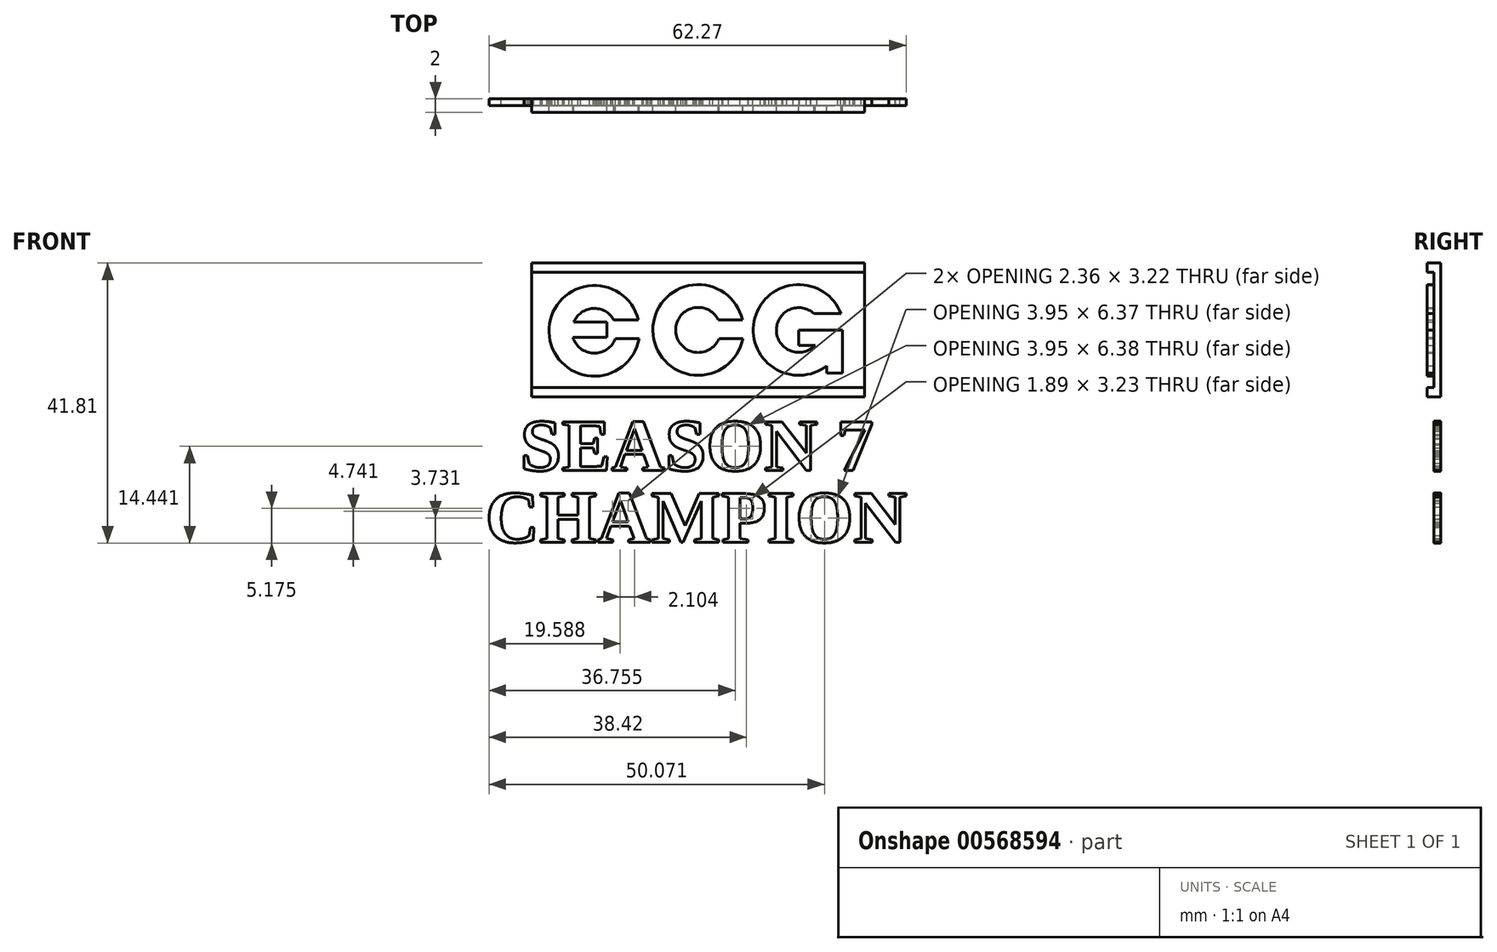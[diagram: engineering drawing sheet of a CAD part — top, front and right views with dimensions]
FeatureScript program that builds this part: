
annotation { "Feature Type Name" : "Feature", "Feature Type Description" : "" }
export const myFeature = defineFeature(function(context is Context, id is Id, definition is map)
    precondition{}
    {
        {
            var Q0;
            Q0=qCreatedBy(makeId("Front.planeOp"),FACE);
            var sketch = newSketch(context, id + "F0", { "sketchPlane" : qUnion([Q0])});
            skArc(sketch, "E0", {"start": v(-20.49, -35.74) * mm, "mid": v(-33.84, -37.62) * mm, "end": v(-20.4, -38.57) * mm});
            skArc(sketch, "E1", {"start": v(-4.95, -35.74) * mm, "mid": v(-18.33, -37.37) * mm, "end": v(-4.9, -38.57) * mm});
            skArc(sketch, "E2", {"start": v(9.79, -34.84) * mm, "mid": v(-3.08, -35.45) * mm, "end": v(7.63, -42.6) * mm});
            skArc(sketch, "E3", {"start": v(-30.27, -38.34) * mm, "mid": v(-27.19, -40.73) * mm, "end": v(-23.94, -38.57) * mm});
            skArc(sketch, "E4", {"start": v(-8.55, -35.74) * mm, "mid": v(-14.92, -37.38) * mm, "end": v(-8.45, -38.57) * mm});
            skLineSegment(sketch, "E5", {"start": v(-25.17, -36.06) * mm, "end": v(-25.17, -38.34) * mm});
            skLineSegment(sketch, "E6", {"start": v(3.45, -37.26) * mm, "end": v(3.45, -39.54) * mm});
            skLineSegment(sketch, "E7", {"start": v(7.63, -43.72) * mm, "end": v(9.99, -43.72) * mm});
            skLineSegment(sketch, "E8", {"start": v(-8.55, -35.74) * mm, "end": v(-4.95, -35.74) * mm});
            skLineSegment(sketch, "E9", {"start": v(-4.9, -38.57) * mm, "end": v(-8.45, -38.57) * mm});
            skLineSegment(sketch, "E10", {"start": v(-25.17, -36.06) * mm, "end": v(-30.13, -36.06) * mm});
            skLineSegment(sketch, "E11", {"start": v(-25.17, -38.34) * mm, "end": v(-30.27, -38.34) * mm});
            skLineSegment(sketch, "E12", {"start": v(-20.49, -35.74) * mm, "end": v(-24.16, -35.74) * mm});
            skLineSegment(sketch, "E13", {"start": v(-20.4, -38.57) * mm, "end": v(-23.94, -38.57) * mm});
            skArc(sketch, "E14.trimOffspring", {"start": v(-24.16, -35.74) * mm, "mid": v(-27.24, -34.05) * mm, "end": v(-30.13, -36.06) * mm});
            skArc(sketch, "E15", {"start": v(5.75, -34.84) * mm, "mid": v(0.12, -37.37) * mm, "end": v(5.9, -39.54) * mm});
            skLineSegment(sketch, "E16", {"start": v(6.8, -37.26) * mm, "end": v(3.45, -37.26) * mm});
            skLineSegment(sketch, "E17", {"start": v(3.45, -39.54) * mm, "end": v(5.9, -39.54) * mm});
            skLineSegment(sketch, "E18", {"start": v(5.75, -34.84) * mm, "end": v(9.79, -34.84) * mm});
            skLineSegment(sketch, "E19", {"start": v(6.8, -37.26) * mm, "end": v(9.99, -37.26) * mm});
            skLineSegment(sketch, "E20", {"start": v(9.99, -37.26) * mm, "end": v(9.99, -43.72) * mm});
            skLineSegment(sketch, "E21", {"start": v(7.63, -43.72) * mm, "end": v(7.63, -42.6) * mm});
            skLineSegment(sketch, "E22.bottom", {"start": v(13.3, -47.26) * mm, "end": v(-36.41, -47.26) * mm});
            skLineSegment(sketch, "E22.top", {"start": v(13.3, -27.26) * mm, "end": v(-36.41, -27.26) * mm});
            skLineSegment(sketch, "E22.left", {"start": v(13.3, -47.26) * mm, "end": v(13.3, -27.26) * mm});
            skLineSegment(sketch, "E22.right", {"start": v(-36.41, -47.26) * mm, "end": v(-36.41, -27.26) * mm});
            skLineSegment(sketch, "E23.bottom", {"start": v(13.3, -45.88) * mm, "end": v(-36.41, -45.88) * mm});
            skLineSegment(sketch, "E23.top", {"start": v(13.3, -28.65) * mm, "end": v(-36.41, -28.65) * mm});
            skLineSegment(sketch, "E23.left", {"start": v(13.3, -45.88) * mm, "end": v(13.3, -28.65) * mm});
            skLineSegment(sketch, "E23.right", {"start": v(-36.41, -45.88) * mm, "end": v(-36.41, -28.65) * mm});
            skPoint(sketch, "E24.middle", {"position": v(-11.55, -47.26) * mm});
            skText(sketch, "E25", { "text": "SEASON 7\n", "fontName": "Tinos-Bold.ttf"});
            skText(sketch, "E26", { "text": "CHAMPION", "fontName": "Tinos-Bold.ttf"});
            skLineSegment(sketch, "E27.bottom", {"start": v(-44.95, -70.25) * mm, "end": v(21.96, -70.25) * mm});
            skLineSegment(sketch, "E27.top", {"start": v(-44.95, -25.99) * mm, "end": v(21.96, -25.99) * mm});
            skLineSegment(sketch, "E27.left", {"start": v(-44.95, -70.25) * mm, "end": v(-44.95, -25.99) * mm});
            skLineSegment(sketch, "E27.right", {"start": v(21.96, -70.25) * mm, "end": v(21.96, -25.99) * mm});
            const initialGuessF0  = {"E25": [-0.03814, -0.05825, 1, 0, 0.008], "E26": [-0.04332, -0.06896, 1, 0, 0.008]};
            skSetInitialGuess(sketch, initialGuessF0);
            skSolve(sketch);
        }
        {
            var Q0;
            Q0=makeQuery(id+"F0.imprint","IMPRINT",FACE,{"disambiguationData":[TD([[makeQuery(id+"F0.imprint","IMPRINT",EDGE,{"derivedFrom":sQuery(id+"F0.wireOp",EDGE,"E25.sketch_text.stroke-0")}),-1.0]])]});
            var Q1;
            Q1=makeQuery(id+"F0.imprint","IMPRINT",FACE,{"disambiguationData":[TD([[makeQuery(id+"F0.imprint","IMPRINT",EDGE,{"derivedFrom":sQuery(id+"F0.wireOp",EDGE,"E25.sketch_text.stroke-29")}),-1.0]])]});
            var Q2;
            Q2=makeQuery(id+"F0.imprint","IMPRINT",FACE,{"disambiguationData":[TD([[makeQuery(id+"F0.imprint","IMPRINT",EDGE,{"derivedFrom":sQuery(id+"F0.wireOp",EDGE,"E25.sketch_text.stroke-55")}),-1.0]])]});
            var Q3;
            Q3=makeQuery(id+"F0.imprint","IMPRINT",FACE,{"disambiguationData":[TD([[makeQuery(id+"F0.imprint","IMPRINT",EDGE,{"derivedFrom":sQuery(id+"F0.wireOp",EDGE,"E25.sketch_text.stroke-74")}),-1.0]])]});
            var Q4;
            Q4=makeQuery(id+"F0.imprint","IMPRINT",FACE,{"disambiguationData":[TD([[makeQuery(id+"F0.imprint","IMPRINT",EDGE,{"derivedFrom":sQuery(id+"F0.wireOp",EDGE,"E25.sketch_text.stroke-103")}),-1.0]])]});
            var Q5;
            Q5=makeQuery(id+"F0.imprint","IMPRINT",FACE,{"disambiguationData":[TD([[makeQuery(id+"F0.imprint","IMPRINT",EDGE,{"derivedFrom":sQuery(id+"F0.wireOp",EDGE,"E25.sketch_text.stroke-118")}),-1.0]])]});
            var Q6;
            Q6=makeQuery(id+"F0.imprint","IMPRINT",FACE,{"disambiguationData":[TD([[makeQuery(id+"F0.imprint","IMPRINT",EDGE,{"derivedFrom":sQuery(id+"F0.wireOp",EDGE,"E25.sketch_text.stroke-138")}),-1.0]])]});
            var Q7;
            Q7=makeQuery(id+"F0.imprint","IMPRINT",FACE,{"disambiguationData":[TD([[makeQuery(id+"F0.imprint","IMPRINT",EDGE,{"derivedFrom":sQuery(id+"F0.wireOp",EDGE,"E26.sketch_text.stroke-140")}),-1.0]])]});
            var Q8;
            Q8=makeQuery(id+"F0.imprint","IMPRINT",FACE,{"disambiguationData":[TD([[makeQuery(id+"F0.imprint","IMPRINT",EDGE,{"derivedFrom":sQuery(id+"F0.wireOp",EDGE,"E26.sketch_text.stroke-125")}),-1.0]])]});
            var Q9;
            Q9=makeQuery(id+"F0.imprint","IMPRINT",FACE,{"disambiguationData":[TD([[makeQuery(id+"F0.imprint","IMPRINT",EDGE,{"derivedFrom":sQuery(id+"F0.wireOp",EDGE,"E26.sketch_text.stroke-92")}),-1.0]])]});
            var Q10;
            Q10=makeQuery(id+"F0.imprint","IMPRINT",FACE,{"disambiguationData":[TD([[makeQuery(id+"F0.imprint","IMPRINT",EDGE,{"derivedFrom":sQuery(id+"F0.wireOp",EDGE,"E26.sketch_text.stroke-113")}),-1.0]])]});
            var Q11;
            Q11=makeQuery(id+"F0.imprint","IMPRINT",FACE,{"disambiguationData":[TD([[makeQuery(id+"F0.imprint","IMPRINT",EDGE,{"derivedFrom":sQuery(id+"F0.wireOp",EDGE,"E26.sketch_text.stroke-67")}),-1.0]])]});
            var Q12;
            Q12=makeQuery(id+"F0.imprint","IMPRINT",FACE,{"disambiguationData":[TD([[makeQuery(id+"F0.imprint","IMPRINT",EDGE,{"derivedFrom":sQuery(id+"F0.wireOp",EDGE,"E26.sketch_text.stroke-48")}),-1.0]])]});
            var Q13;
            Q13=makeQuery(id+"F0.imprint","IMPRINT",FACE,{"disambiguationData":[TD([[makeQuery(id+"F0.imprint","IMPRINT",EDGE,{"derivedFrom":sQuery(id+"F0.wireOp",EDGE,"E26.sketch_text.stroke-20")}),-1.0]])]});
            var Q14;
            Q14=makeQuery(id+"F0.imprint","IMPRINT",FACE,{"disambiguationData":[TD([[makeQuery(id+"F0.imprint","IMPRINT",EDGE,{"derivedFrom":sQuery(id+"F0.wireOp",EDGE,"E26.sketch_text.stroke-0")}),-1.0]])]});
            var Q15;
            {var subQ0=sQuery(id+"F0.wireOp",EDGE,"E22.bottom");Q15=makeQuery(id+"F0.imprint","IMPRINT",FACE,{"disambiguationData":[TD([[makeQuery(id+"F0.imprint","IMPRINT",EDGE,{"derivedFrom":subQ0}),-1.0]])]});}
            var Q16;
            Q16=makeQuery(id+"F0.imprint","IMPRINT",FACE,{"disambiguationData":[TD([[makeQuery(id+"F0.imprint","IMPRINT",EDGE,{"derivedFrom":sQuery(id+"F0.wireOp",EDGE,"E0")}),-1.0]])]});
            var Q17;
            Q17=makeQuery(id+"F0.imprint","IMPRINT",FACE,{"disambiguationData":[TD([[makeQuery(id+"F0.imprint","IMPRINT",EDGE,{"derivedFrom":sQuery(id+"F0.wireOp",EDGE,"E0")}),1.0]])]});
            var Q18;
            Q18=makeQuery(id+"F0.imprint","IMPRINT",FACE,{"disambiguationData":[TD([[makeQuery(id+"F0.imprint","IMPRINT",EDGE,{"derivedFrom":sQuery(id+"F0.wireOp",EDGE,"E1")}),1.0]])]});
            var Q19;
            Q19=makeQuery(id+"F0.imprint","IMPRINT",FACE,{"disambiguationData":[TD([[makeQuery(id+"F0.imprint","IMPRINT",EDGE,{"derivedFrom":sQuery(id+"F0.wireOp",EDGE,"E2")}),1.0]])]});
            var Q20;
            {var subQ0=sQuery(id+"F0.wireOp",EDGE,"E22.top");Q20=makeQuery(id+"F0.imprint","IMPRINT",FACE,{"disambiguationData":[TD([[makeQuery(id+"F0.imprint","IMPRINT",EDGE,{"derivedFrom":subQ0}),1.0]])]});}
            extrude(context, id + "F1", {"entities" : qUnion([Q0, Q1, Q2, Q3, Q4, Q5, Q6, Q7, Q8, Q9, Q10, Q11, Q12, Q13, Q14, Q15, Q16, Q17, Q18, Q19, Q20]), "depth" : 1 * mm, "offsetDistance" : 25 * mm});
        }
        {
            var Q0;
            {var subQ0=sQuery(id+"F0.wireOp",EDGE,"E22.bottom");Q0=makeQuery(id+"F0.imprint","IMPRINT",FACE,{"disambiguationData":[TD([[makeQuery(id+"F0.imprint","IMPRINT",EDGE,{"derivedFrom":subQ0}),-1.0]])]});}
            var Q1;
            {var subQ0=sQuery(id+"F0.wireOp",EDGE,"E22.top");Q1=makeQuery(id+"F0.imprint","IMPRINT",FACE,{"disambiguationData":[TD([[makeQuery(id+"F0.imprint","IMPRINT",EDGE,{"derivedFrom":subQ0}),1.0]])]});}
            var Q2;
            Q2=makeQuery(id+"F0.imprint","IMPRINT",FACE,{"disambiguationData":[TD([[makeQuery(id+"F0.imprint","IMPRINT",EDGE,{"derivedFrom":sQuery(id+"F0.wireOp",EDGE,"E2")}),1.0]])]});
            var Q3;
            Q3=makeQuery(id+"F0.imprint","IMPRINT",FACE,{"disambiguationData":[TD([[makeQuery(id+"F0.imprint","IMPRINT",EDGE,{"derivedFrom":sQuery(id+"F0.wireOp",EDGE,"E1")}),1.0]])]});
            var Q4;
            Q4=makeQuery(id+"F0.imprint","IMPRINT",FACE,{"disambiguationData":[TD([[makeQuery(id+"F0.imprint","IMPRINT",EDGE,{"derivedFrom":sQuery(id+"F0.wireOp",EDGE,"E0")}),1.0]])]});
            extrude(context, id + "F2", {"entities" : qUnion([Q0, Q1, Q2, Q3, Q4]), "operationType" : NewBodyOperationType.ADD, "depth" : 2 * mm, "offsetDistance" : 25 * mm});
        }
    });
